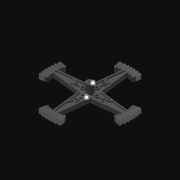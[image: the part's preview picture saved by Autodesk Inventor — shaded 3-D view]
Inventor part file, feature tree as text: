
AUTODESK INVENTOR PART (.ipt)
format: ipt  version: 2021 (Build 250183000, 183)  size: 1,061,888 bytes
history: native  units: in
note: dims shown in document units (in); Inventor stores cm internally (conversion verified against a paired STEP export)
features: other x2, split x1, imported_body x1, sketch x1
ambient origin geometry x8: Origin, YZ Plane, XZ Plane, XY Plane, X Axis, Y Axis, Z Axis, Center Point
bodies: Body1 (feature_tree)
feature tree (5):
  parser-record x1  (decoder bookkeeping rows leaked as tree rows — omitted from the tree; the rows remain in map.json)
  other  "276-2218-STEP1"
  split  "Split1"
  imported_body  "Base1"
  sketch  "Sketch1"  dims[d0=0.0in d1=0.0in]
